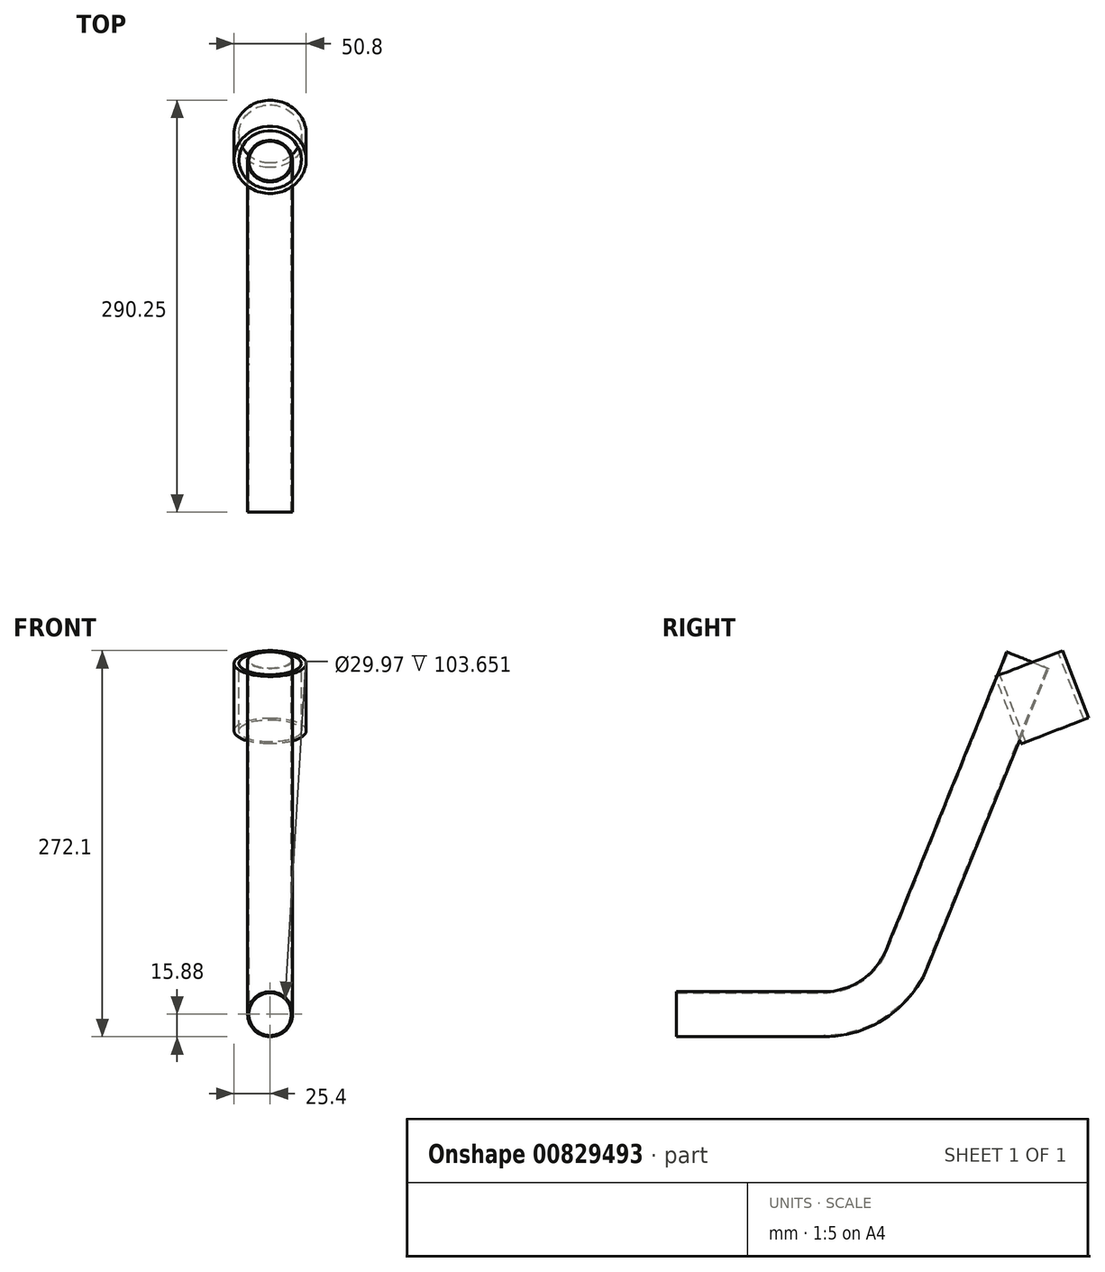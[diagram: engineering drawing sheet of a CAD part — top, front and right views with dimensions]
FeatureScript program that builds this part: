
annotation { "Feature Type Name" : "Feature", "Feature Type Description" : "" }
export const myFeature = defineFeature(function(context is Context, id is Id, definition is map)
    precondition{}
    {
        {
            var Q0;
            Q0=qCreatedBy(makeId("Right.planeOp"),FACE);
            var sketch = newSketch(context, id + "F0", { "sketchPlane" : qUnion([Q0])});
            skCircle(sketch, "E0", {"center": v(0, 0) * mm, "radius": 152.4 * mm});
            skCircle(sketch, "E1", {"center": v(-520, 0) * mm, "radius": 152.4 * mm});
            skLineSegment(sketch, "E2", {"start": v(0, 0) * mm, "end": v(-4.67, -1.8) * mm});
            skLineSegment(sketch, "E3", {"start": v(-4.67, -1.8) * mm, "end": v(-59.25, 140.4) * mm});
            skLineSegment(sketch, "E4", {"start": v(0, 0) * mm, "end": v(-520, 0) * mm, "construction": true});
            skLineSegment(sketch, "E5", {"start": v(-59.25, 140.4) * mm, "end": v(-82.01, 199.7) * mm});
            skLineSegment(sketch, "E6", {"start": v(-82.01, 199.7) * mm, "end": v(-100.22, 247.12) * mm});
            skLineSegment(sketch, "E7", {"start": v(-101.1, 249.4) * mm, "end": v(-186.04, 39.66) * mm});
            skLineSegment(sketch, "E8", {"start": v(-173.62, 70.32) * mm, "end": v(-141.25, 57.21) * mm});
            skLineSegment(sketch, "E9", {"start": v(-348.55, 0) * mm, "end": v(-244.9, 0) * mm});
            skLineSegment(sketch, "E10", {"start": v(-348.55, 0) * mm, "end": v(-367.6, 0) * mm});
            skLineSegment(sketch, "E11", {"start": v(-348.55, 0) * mm, "end": v(-520, 0) * mm});
            skLineSegment(sketch, "E12", {"start": v(-520, 0) * mm, "end": v(-316.75, 48.63) * mm});
            skLineSegment(sketch, "E13", {"start": v(-316.75, 48.63) * mm, "end": v(-300, 0) * mm});
            skPoint(sketch, "E14", {"position": v(-101.1, 249.4) * mm});
            skLineSegment(sketch, "E15", {"start": v(-316.75, 48.63) * mm, "end": v(-182.4, 48.63) * mm});
            skPoint(sketch, "E16", {"position": v(-520, -152.4) * mm});
            skLineSegment(sketch, "E17", {"start": v(-162.65, 139.7) * mm, "end": v(-115.8, 255.36) * mm, "construction": true});
            skLineSegment(sketch, "E18", {"start": v(-115.8, 255.36) * mm, "end": v(-101.1, 249.4) * mm, "construction": true});
            skLineSegment(sketch, "E19", {"start": v(-158.91, 64.36) * mm, "end": v(-92.76, 227.7) * mm, "construction": true});
            skLineSegment(sketch, "E20", {"start": v(-123.93, 238.01) * mm, "end": v(-105.72, 190.59) * mm, "construction": true});
            skLineSegment(sketch, "E21", {"start": v(-123.93, 238.01) * mm, "end": v(-100.22, 247.12) * mm, "construction": true});
            skLineSegment(sketch, "E22", {"start": v(-105.72, 190.59) * mm, "end": v(-82.01, 199.7) * mm, "construction": true});
            skPoint(sketch, "E23.visualSharp", {"position": v(-202.1, 0) * mm});
            skArc(sketch, "E23.filletArc", {"start": v(-244.9, 0) * mm, "mid": v(-209.41, 10.84) * mm, "end": v(-186.04, 39.66) * mm});
            skSolve(sketch);
        }
        {
            var Q0;
            Q0=sQuery(id+"F0.wireOp",EDGE,"E6");
            var Q1;
            Q1=sQuery(id+"F0.wireOp",VERTEX,"E6.end");
            cPlane(context, id + "F1", {"entities" : qUnion([Q0, Q1]), "cplaneType" : CPlaneType.LINE_POINT, "offset" : 25.4 * mm, "width" : 152.4 * mm, "height" : 152.4 * mm});
        }
        {
            var Q0;
            Q0=qCreatedBy(id+"F1.planeOp",FACE);
            var sketch = newSketch(context, id + "F2", { "sketchPlane" : qUnion([Q0])});
            skCircle(sketch, "E24", {"center": v(0, -5) * mm, "radius": 22 * mm});
            skCircle(sketch, "E25", {"center": v(0, -5) * mm, "radius": 25.4 * mm});
            skSolve(sketch);
        }
        {
            var Q0;
            Q0=makeQuery(id+"F2.imprint","IMPRINT",FACE,{"disambiguationData":[TD([[makeQuery(id+"F2.imprint","IMPRINT",EDGE,{"derivedFrom":sQuery(id+"F2.wireOp",EDGE,"E24")}),-1.0]])]});
            var Q1;
            Q1=sQuery(id+"F0.wireOp",VERTEX,"E5.end");
            extrude(context, id + "F3", {"entities" : qUnion([Q0]), "endBound" : BoundingType.UP_TO_VERTEX, "oppositeDirection" : true, "depth" : 25.4 * mm, "endBoundEntityVertex" : qUnion([Q1]), "offsetDistance" : 25.4 * mm});
        }
        {
            var Q0;
            Q0=sQuery(id+"F0.wireOp",VERTEX,"E9.start");
            var Q1;
            Q1=sQuery(id+"F0.wireOp",EDGE,"E9");
            cPlane(context, id + "F4", {"entities" : qUnion([Q0, Q1]), "cplaneType" : CPlaneType.LINE_POINT, "offset" : 25.4 * mm, "width" : 152.4 * mm, "height" : 152.4 * mm});
        }
        {
            var Q0;
            Q0=qCreatedBy(id+"F4.planeOp",FACE);
            var sketch = newSketch(context, id + "F5", { "sketchPlane" : qUnion([Q0])});
            skCircle(sketch, "E26", {"center": v(0, 0) * mm, "radius": 15.88 * mm});
            skCircle(sketch, "E27", {"center": v(0, 0) * mm, "radius": 14.99 * mm});
            skSolve(sketch);
        }
        {
            var Q0;
            Q0=qCreatedBy(makeId("Right.planeOp"),FACE);
            var sketch = newSketch(context, id + "F6", { "sketchPlane" : qUnion([Q0])});
            skLineSegment(sketch, "E28.0", {"start": v(-348.55, 0) * mm, "end": v(-244.9, 0) * mm});
            skArc(sketch, "E28.1", {"start": v(-244.9, 0) * mm, "mid": v(-209.41, 10.84) * mm, "end": v(-186.04, 39.66) * mm});
            skLineSegment(sketch, "E28.2", {"start": v(-101.1, 249.4) * mm, "end": v(-186.04, 39.66) * mm});
            skSolve(sketch);
        }
        {
            var Q0;
            Q0=makeQuery(id+"F5.imprint","IMPRINT",FACE,{"disambiguationData":[TD([[makeQuery(id+"F5.imprint","IMPRINT",EDGE,{"derivedFrom":sQuery(id+"F5.wireOp",EDGE,"E26")}),1.0]])]});
            var Q1;
            Q1 = qConstructionFilter(qBodyType(qCreatedBy(id + "F6" ,EDGE), BodyType.WIRE), ConstructionObject.NO);
            sweep(context, id + "F7", {"profiles" : qUnion([Q0]), "path" : qUnion([Q1])});
        }
    });
